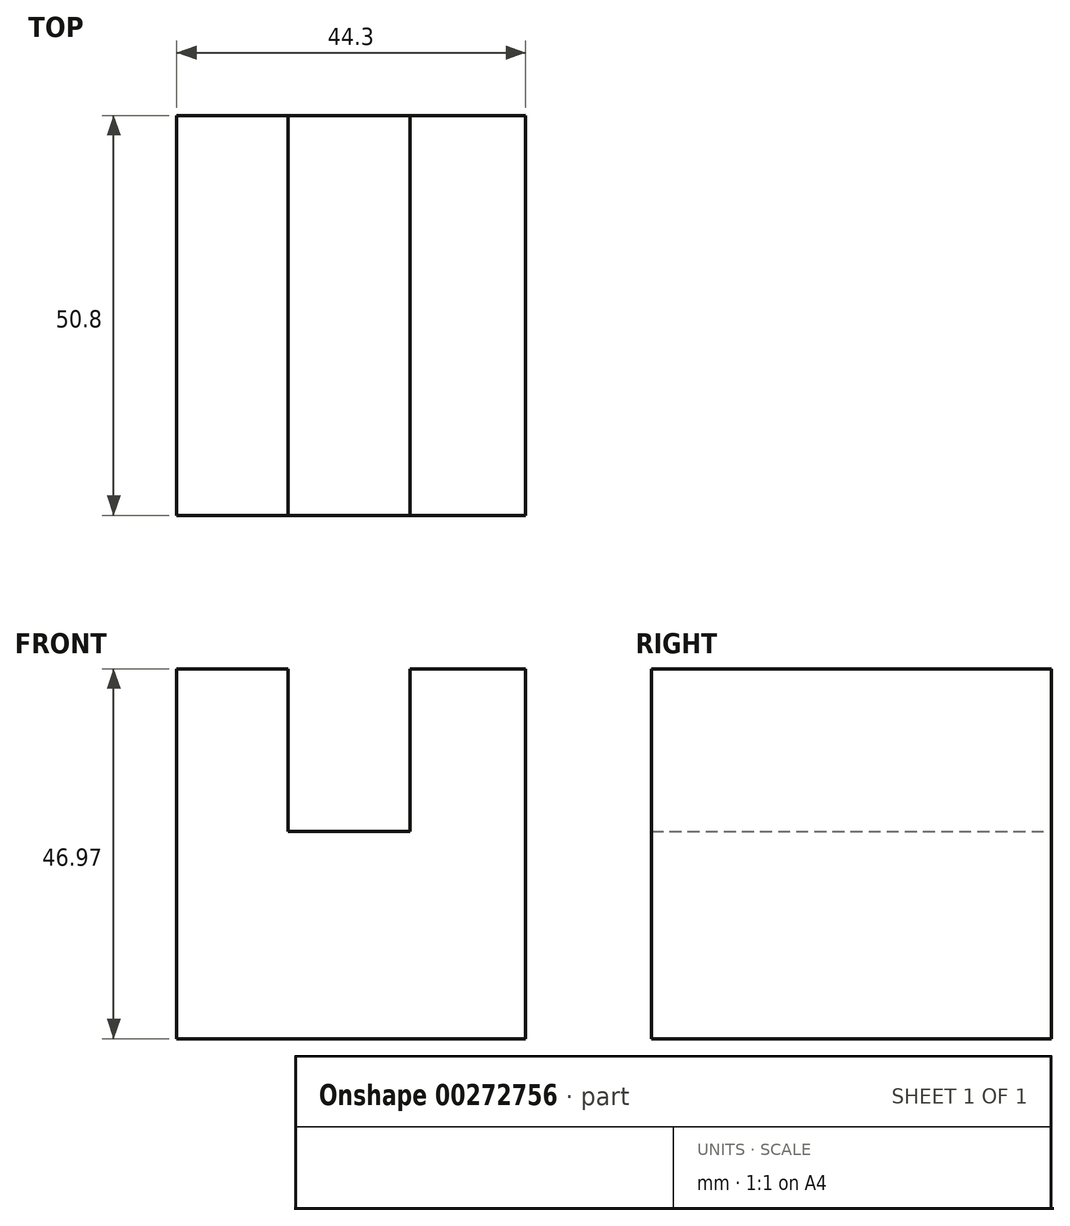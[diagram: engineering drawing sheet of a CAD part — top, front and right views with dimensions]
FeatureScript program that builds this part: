
annotation { "Feature Type Name" : "Feature", "Feature Type Description" : "" }
export const myFeature = defineFeature(function(context is Context, id is Id, definition is map)
    precondition{}
    {
        {
            var Q0;
            Q0=qCreatedBy(makeId("Front.planeOp"),FACE);
            var sketch = newSketch(context, id + "F0", { "sketchPlane" : qUnion([Q0])});
            skLineSegment(sketch, "E0", {"start": v(-62.44, 46.97) * mm, "end": v(-62.44, 0) * mm});
            skLineSegment(sketch, "E1", {"start": v(-62.44, 46.97) * mm, "end": v(-48.31, 46.97) * mm});
            skLineSegment(sketch, "E2", {"start": v(-48.31, 46.97) * mm, "end": v(-48.31, 26.35) * mm});
            skLineSegment(sketch, "E3", {"start": v(-48.31, 26.35) * mm, "end": v(-32.84, 26.35) * mm});
            skLineSegment(sketch, "E4", {"start": v(-32.84, 26.35) * mm, "end": v(-32.84, 46.97) * mm});
            skLineSegment(sketch, "E5", {"start": v(-32.84, 46.97) * mm, "end": v(-18.14, 46.97) * mm});
            skLineSegment(sketch, "E6", {"start": v(-18.14, 46.97) * mm, "end": v(-18.14, 0) * mm});
            skLineSegment(sketch, "E7", {"start": v(-18.14, 0) * mm, "end": v(-62.44, 0) * mm});
            skSolve(sketch);
        }
        {
            var Q0;
            Q0=makeQuery(id+"F0.imprint","IMPRINT",FACE,{"disambiguationData":[TD([[makeQuery(id+"F0.imprint","IMPRINT",EDGE,{"derivedFrom":sQuery(id+"F0.wireOp",EDGE,"E0")}),1.0]])]});
            extrude(context, id + "F1", {"entities" : qUnion([Q0]), "depth" : 50.8 * mm});
        }
    });
